SOLIDWORKS PART (.sldprt)
format: sldprt  version: not decoded by parser v0  size: 88,064 bytes
history: native  units: mm
features: sketch x8, cut_extrude x6, extrude x2 + 2 further entries (+8 scaffold rows collapsed; 3 parser-record rows omitted)
feature tree (29):
  scaffold x8  (default folders/planes/origin — collapsed)
  parser-record x3  (decoder bookkeeping rows leaked as tree rows — omitted from the tree; the rows remain in map.json)
  "ID2"
  "ID3"
  sketch  "Sketch1"  dims[D1=50.8mm D2=25.4mm]
  extrude  "Base-Extrude"  Depth=2.032mm
  sketch  "Sketch2"  dims[c1.D1=6.5278mm c1.D2=6.5278mm c1.D3=6.5278mm c2.D2=11.9126mm c2.D3=12.7mm]
  cut_extrude  "Cut-Extrude1"  [1 undecoded]
  sketch  "Sketch3"  dims[c1.D1=6.5278mm c1.D2=6.5278mm c1.D3=6.5278mm c2.D2=12.7mm c2.D3=11.9126mm]
  cut_extrude  "Cut-Extrude2"  [1 undecoded]
  sketch  "Sketch7"  dims[D1=9.1948mm D2=25.4mm]
  extrude  "Boss-Extrude2"  [1 undecoded]
  sketch  "Sketch8"  dims[D1=5.1308mm]
  cut_extrude  "Cut-Extrude3"  [1 undecoded]
  sketch  "Sketch10"  dims[D1=8.89mm]
  cut_extrude  "Cut-Extrude5"  [1 undecoded]
  sketch  "Sketch11"  dims[D1=8.89mm]
  cut_extrude  "Cut-Extrude6"  [1 undecoded]
  sketch  "Sketch12"  dims[D1=8.89mm D2=8.89mm]
  cut_extrude  "Cut-Extrude7"  [1 undecoded]
decode coverage: 9 of 16 modeling features carry decoded parameters; 2 rows unclassified (native names shown)
note: 7 parameter values undecoded
summary: no parameter record found for 7 features
note: suppression state not decoded; provenance and decode notes live in map.json
